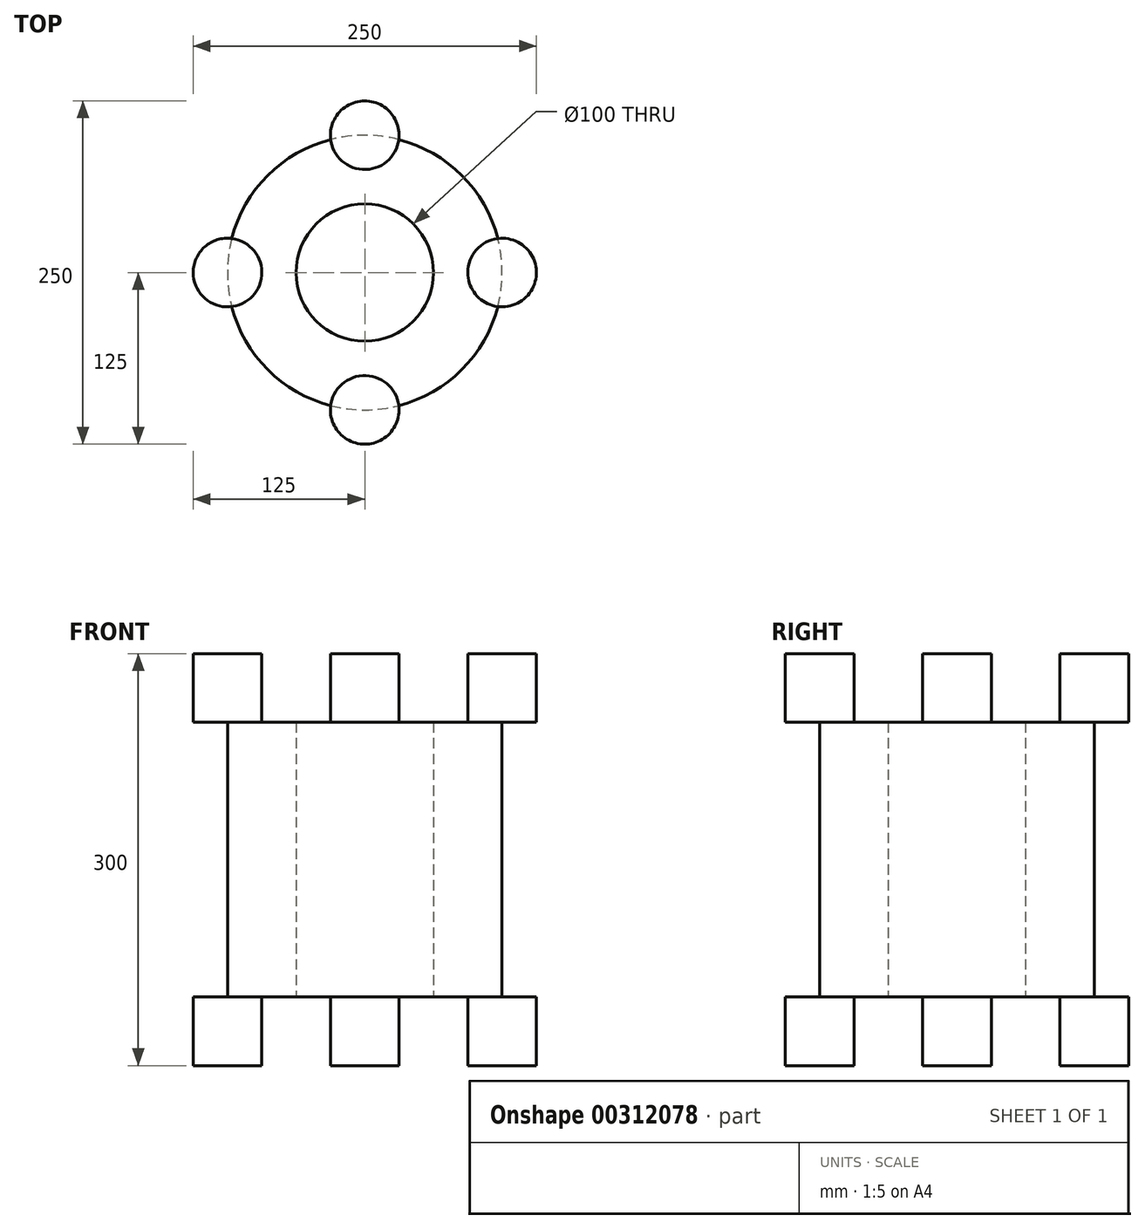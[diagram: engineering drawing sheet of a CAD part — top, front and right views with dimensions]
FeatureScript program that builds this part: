
annotation { "Feature Type Name" : "Feature", "Feature Type Description" : "" }
export const myFeature = defineFeature(function(context is Context, id is Id, definition is map)
    precondition{}
    {
        {
            var Q0;
            Q0=qCreatedBy(makeId("Front.planeOp"),FACE);
            var sketch = newSketch(context, id + "F0", { "sketchPlane" : qUnion([Q0])});
            skLineSegment(sketch, "E0.bottom", {"start": v(0, -100) * mm, "end": v(-100, -100) * mm});
            skLineSegment(sketch, "E0.top", {"start": v(0, 100) * mm, "end": v(-100, 100) * mm});
            skLineSegment(sketch, "E0.left", {"start": v(0, -100) * mm, "end": v(0, 100) * mm});
            skLineSegment(sketch, "E0.right", {"start": v(-100, -100) * mm, "end": v(-100, 100) * mm});
            skLineSegment(sketch, "E1", {"start": v(0, 0) * mm, "end": v(-100, 0) * mm, "construction": true});
            skSolve(sketch);
        }
        {
            var Q0;
            Q0=makeQuery(id+"F0.imprint","IMPRINT",FACE,{"disambiguationData":[TD([[makeQuery(id+"F0.imprint","IMPRINT",EDGE,{"derivedFrom":sQuery(id+"F0.wireOp",EDGE,"E0.bottom")}),-1.0]])]});
            var Q1;
            Q1=sQuery(id+"F0.wireOp",EDGE,"E0.left");
            revolve(context, id + "F1", {"entities" : qUnion([Q0]), "axis" : qUnion([Q1]), "revolveType" : RevolveType.FULL});
        }
        {
            var Q0;
            Q0=makeQuery(id+"F1.opRevolve","SWEPT_FACE",FACE,{"disambiguationData":[OSD([sQuery(id+"F0.wireOp",EDGE,"E0.bottom")])]});
            var sketch = newSketch(context, id + "F2", { "sketchPlane" : qUnion([Q0])});
            skCircle(sketch, "E2", {"center": v(0, 0) * mm, "radius": 50 * mm});
            skSolve(sketch);
        }
        {
            var Q0;
            Q0 = qSketchRegion(id + "F2", true);
            extrude(context, id + "F3", {"entities" : qUnion([Q0]), "operationType" : NewBodyOperationType.REMOVE, "oppositeDirection" : true, "depth" : 200 * mm});
        }
        {
            var Q0;
            Q0=makeQuery(id+"F1.opRevolve","SWEPT_FACE",FACE,{"disambiguationData":[OSD([sQuery(id+"F0.wireOp",EDGE,"E0.bottom")])]});
            var sketch = newSketch(context, id + "F4", { "sketchPlane" : qUnion([Q0])});
            skCircle(sketch, "E3", {"center": v(0, -100) * mm, "radius": 25 * mm});
            skCircle(sketch, "E4", {"center": v(100, 0) * mm, "radius": 25 * mm});
            skCircle(sketch, "E5", {"center": v(0, 100) * mm, "radius": 25 * mm});
            skCircle(sketch, "E6", {"center": v(-100, 0) * mm, "radius": 25 * mm});
            skSolve(sketch);
        }
        {
            var Q0;
            {var subQ0=sQuery(id+"F4.wireOp",EDGE,"E6");var subQ1=makeQuery(id+"F1.opRevolve","SWEPT_EDGE",EDGE,{"disambiguationData":[OSD([sQuery(id+"F0.wireOp",EDGE,"E0.bottom"),sQuery(id+"F0.wireOp",EDGE,"E0.right")])]});var subQ2=makeQuery(id+"F4.imprint","INTERSECT",VERTEX,{"disambiguationData":[OD(0.0)],"derivedFrom":[subQ1,subQ0]});Q0=makeQuery(id+"F4.imprint","IMPRINT",FACE,{"disambiguationData":[TD([[makeQuery(id+"F4.imprint","IMPRINT",EDGE,{"disambiguationData":[TD([[subQ2,-1.0]])],"derivedFrom":subQ0}),1.0]])]});}
            var Q1;
            {var subQ0=sQuery(id+"F4.wireOp",EDGE,"E6");var subQ1=makeQuery(id+"F1.opRevolve","SWEPT_EDGE",EDGE,{"disambiguationData":[OSD([sQuery(id+"F0.wireOp",EDGE,"E0.bottom"),sQuery(id+"F0.wireOp",EDGE,"E0.right")])]});var subQ2=makeQuery(id+"F4.imprint","INTERSECT",VERTEX,{"disambiguationData":[OD(0.0)],"derivedFrom":[subQ1,subQ0]});Q1=makeQuery(id+"F4.imprint","IMPRINT",FACE,{"disambiguationData":[TD([[makeQuery(id+"F4.imprint","IMPRINT",EDGE,{"disambiguationData":[TD([[subQ2,1.0]])],"derivedFrom":subQ0}),1.0]])]});}
            var Q2;
            {var subQ0=sQuery(id+"F4.wireOp",EDGE,"E3");var subQ1=makeQuery(id+"F1.opRevolve","SWEPT_EDGE",EDGE,{"disambiguationData":[OSD([sQuery(id+"F0.wireOp",EDGE,"E0.bottom"),sQuery(id+"F0.wireOp",EDGE,"E0.right")])]});var subQ2=makeQuery(id+"F4.imprint","INTERSECT",VERTEX,{"disambiguationData":[OD(0.0)],"derivedFrom":[subQ1,subQ0]});Q2=makeQuery(id+"F4.imprint","IMPRINT",FACE,{"disambiguationData":[TD([[makeQuery(id+"F4.imprint","IMPRINT",EDGE,{"disambiguationData":[TD([[subQ2,1.0]])],"derivedFrom":subQ0}),1.0]])]});}
            var Q3;
            {var subQ0=sQuery(id+"F4.wireOp",EDGE,"E3");var subQ1=makeQuery(id+"F1.opRevolve","SWEPT_EDGE",EDGE,{"disambiguationData":[OSD([sQuery(id+"F0.wireOp",EDGE,"E0.bottom"),sQuery(id+"F0.wireOp",EDGE,"E0.right")])]});var subQ2=makeQuery(id+"F4.imprint","INTERSECT",VERTEX,{"disambiguationData":[OD(0.0)],"derivedFrom":[subQ1,subQ0]});Q3=makeQuery(id+"F4.imprint","IMPRINT",FACE,{"disambiguationData":[TD([[makeQuery(id+"F4.imprint","IMPRINT",EDGE,{"disambiguationData":[TD([[subQ2,-1.0]])],"derivedFrom":subQ0}),1.0]])]});}
            var Q4;
            {var subQ0=sQuery(id+"F4.wireOp",EDGE,"E5");var subQ1=makeQuery(id+"F1.opRevolve","SWEPT_EDGE",EDGE,{"disambiguationData":[OSD([sQuery(id+"F0.wireOp",EDGE,"E0.bottom"),sQuery(id+"F0.wireOp",EDGE,"E0.right")])]});var subQ2=makeQuery(id+"F4.imprint","INTERSECT",VERTEX,{"disambiguationData":[OD(0.0)],"derivedFrom":[subQ1,subQ0]});Q4=makeQuery(id+"F4.imprint","IMPRINT",FACE,{"disambiguationData":[TD([[makeQuery(id+"F4.imprint","IMPRINT",EDGE,{"disambiguationData":[TD([[subQ2,1.0]])],"derivedFrom":subQ0}),1.0]])]});}
            var Q5;
            {var subQ0=sQuery(id+"F4.wireOp",EDGE,"E5");var subQ1=makeQuery(id+"F1.opRevolve","SWEPT_EDGE",EDGE,{"disambiguationData":[OSD([sQuery(id+"F0.wireOp",EDGE,"E0.bottom"),sQuery(id+"F0.wireOp",EDGE,"E0.right")])]});var subQ2=makeQuery(id+"F4.imprint","INTERSECT",VERTEX,{"disambiguationData":[OD(0.0)],"derivedFrom":[subQ1,subQ0]});Q5=makeQuery(id+"F4.imprint","IMPRINT",FACE,{"disambiguationData":[TD([[makeQuery(id+"F4.imprint","IMPRINT",EDGE,{"disambiguationData":[TD([[subQ2,-1.0]])],"derivedFrom":subQ0}),1.0]])]});}
            var Q6;
            {var subQ0=sQuery(id+"F4.wireOp",EDGE,"E4");var subQ1=makeQuery(id+"F1.opRevolve","SWEPT_EDGE",EDGE,{"disambiguationData":[OSD([sQuery(id+"F0.wireOp",EDGE,"E0.bottom"),sQuery(id+"F0.wireOp",EDGE,"E0.right")])]});var subQ2=makeQuery(id+"F4.imprint","INTERSECT",VERTEX,{"disambiguationData":[OD(0.0)],"derivedFrom":[subQ1,subQ0]});Q6=makeQuery(id+"F4.imprint","IMPRINT",FACE,{"disambiguationData":[TD([[makeQuery(id+"F4.imprint","IMPRINT",EDGE,{"disambiguationData":[TD([[subQ2,-1.0]])],"derivedFrom":subQ0}),1.0]])]});}
            var Q7;
            {var subQ0=sQuery(id+"F4.wireOp",EDGE,"E4");var subQ1=makeQuery(id+"F1.opRevolve","SWEPT_EDGE",EDGE,{"disambiguationData":[OSD([sQuery(id+"F0.wireOp",EDGE,"E0.bottom"),sQuery(id+"F0.wireOp",EDGE,"E0.right")])]});var subQ2=makeQuery(id+"F4.imprint","INTERSECT",VERTEX,{"disambiguationData":[OD(0.0)],"derivedFrom":[subQ1,subQ0]});Q7=makeQuery(id+"F4.imprint","IMPRINT",FACE,{"disambiguationData":[TD([[makeQuery(id+"F4.imprint","IMPRINT",EDGE,{"disambiguationData":[TD([[subQ2,1.0]])],"derivedFrom":subQ0}),1.0]])]});}
            extrude(context, id + "F5", {"entities" : qUnion([Q0, Q1, Q2, Q3, Q4, Q5, Q6, Q7]), "operationType" : NewBodyOperationType.ADD, "depth" : 50 * mm});
        }
        {
            var Q0;
            Q0=makeQuery(id+"F1.opRevolve","SWEPT_BODY",BODY,{"disambiguationData":[OSD([sQuery(id+"F0.wireOp",EDGE,"E0.bottom"),sQuery(id+"F0.wireOp",EDGE,"E0.top"),sQuery(id+"F0.wireOp",EDGE,"E0.left"),sQuery(id+"F0.wireOp",EDGE,"E0.right")])]});
            var Q1;
            Q1=qCreatedBy(makeId("Top.planeOp"),FACE);
            mirror(context, id + "F6", {"operationType" : NewBodyOperationType.ADD, "entities" : qUnion([Q0]), "mirrorPlane" : qUnion([Q1])});
        }
    });
